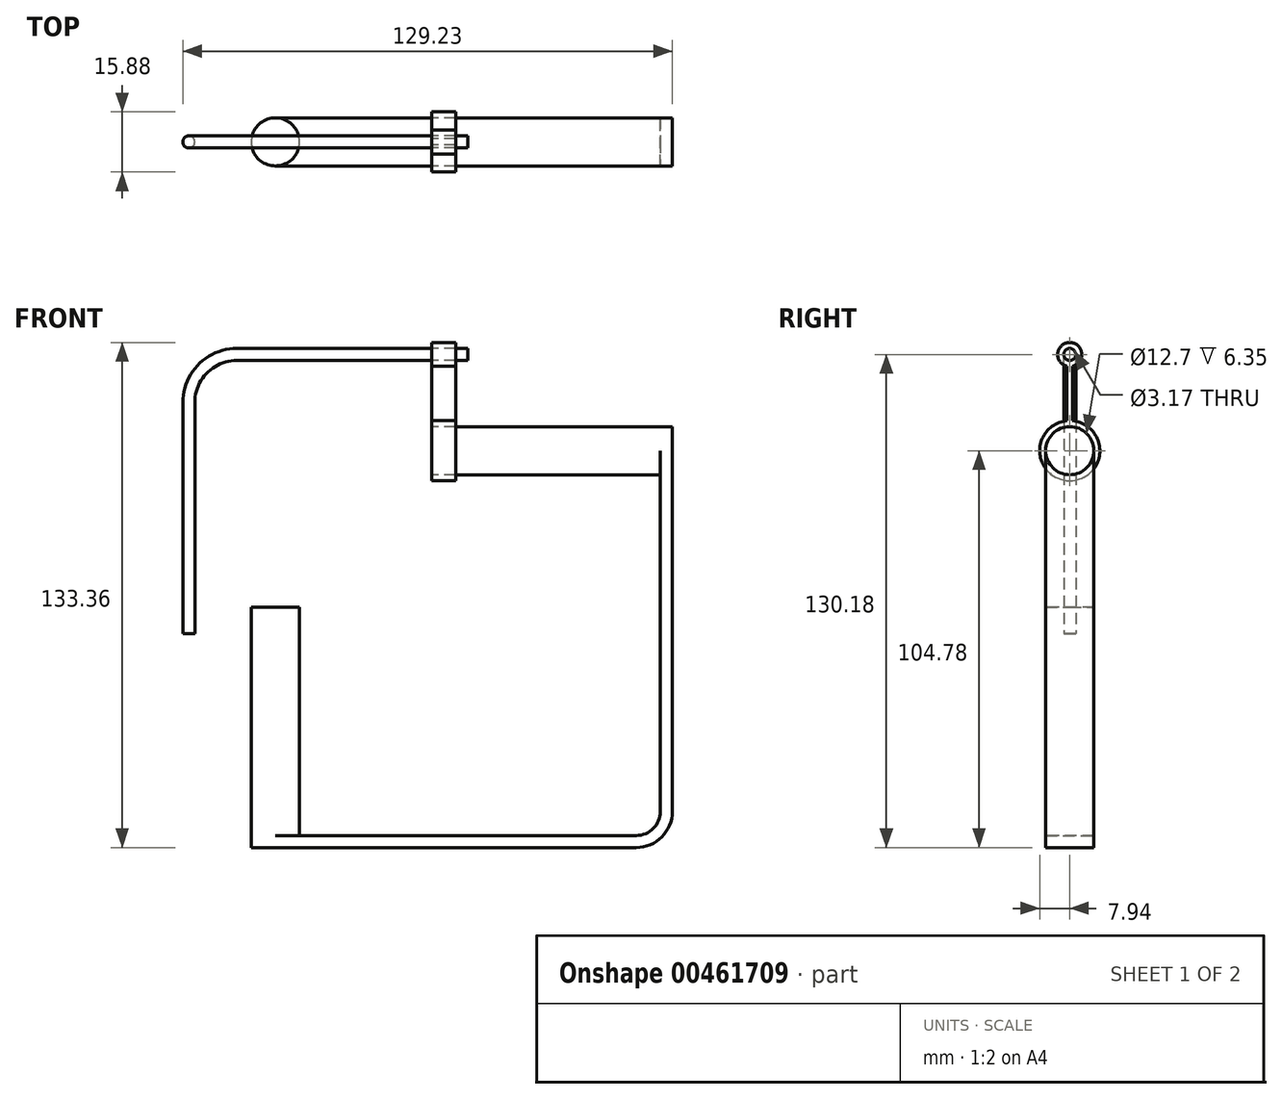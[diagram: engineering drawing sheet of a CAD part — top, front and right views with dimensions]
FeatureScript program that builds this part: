
annotation { "Feature Type Name" : "Feature", "Feature Type Description" : "" }
export const myFeature = defineFeature(function(context is Context, id is Id, definition is map)
    precondition{}
    {
        {
            var Q0;
            Q0=qCreatedBy(makeId("Front.planeOp"),FACE);
            var sketch = newSketch(context, id + "F0", { "sketchPlane" : qUnion([Q0])});
            skLineSegment(sketch, "E0", {"start": v(0, 0) * mm, "end": v(0, 101.6) * mm});
            skLineSegment(sketch, "E1", {"start": v(0, 0) * mm, "end": v(-101.6, 0) * mm});
            skLineSegment(sketch, "E2", {"start": v(0, 101.6) * mm, "end": v(3.17, 101.6) * mm});
            skLineSegment(sketch, "E3", {"start": v(3.17, 101.6) * mm, "end": v(3.18, -3.17) * mm});
            skLineSegment(sketch, "E4", {"start": v(3.18, -3.17) * mm, "end": v(-101.6, -3.18) * mm});
            skLineSegment(sketch, "E5", {"start": v(-101.6, -3.18) * mm, "end": v(-101.6, 0) * mm});
            skSolve(sketch);
        }
        {
            var Q0;
            Q0 = qSketchRegion(id + "F0", true);
            extrude(context, id + "F1", {"entities" : qUnion([Q0]), "endBound" : BoundingType.SYMMETRIC, "depth" : 12.7 * mm});
        }
        {
            var Q0;
            Q0=makeQuery(id+"F1.opExtrude","SWEPT_FACE",FACE,{"disambiguationData":[OSD([sQuery(id+"F0.wireOp",EDGE,"E3")])]});
            var sketch = newSketch(context, id + "F2", { "sketchPlane" : qUnion([Q0])});
            skCircle(sketch, "E6", {"center": v(0, 101.6) * mm, "radius": 6.35 * mm});
            skSolve(sketch);
        }
        {
            var Q0;
            Q0 = qSketchRegion(id + "F2", true);
            extrude(context, id + "F3", {"entities" : qUnion([Q0]), "operationType" : NewBodyOperationType.ADD, "oppositeDirection" : true, "depth" : 63.5 * mm});
        }
        {
            var Q0;
            Q0=makeQuery(id+"F1.opExtrude","SWEPT_FACE",FACE,{"disambiguationData":[OSD([sQuery(id+"F0.wireOp",EDGE,"E4")])]});
            var sketch = newSketch(context, id + "F4", { "sketchPlane" : qUnion([Q0])});
            skCircle(sketch, "E7", {"center": v(-101.6, 0) * mm, "radius": 6.35 * mm});
            skSolve(sketch);
        }
        {
            var Q0;
            Q0 = qSketchRegion(id + "F4", true);
            extrude(context, id + "F5", {"entities" : qUnion([Q0]), "operationType" : NewBodyOperationType.ADD, "oppositeDirection" : true, "depth" : 63.5 * mm});
        }
        {
            var Q0;
            Q0=makeQuery(id+"F3.opExtrude","CAP_FACE",FACE,{"disambiguationData":[OSD([sQuery(id+"F2.wireOp",EDGE,"E6")])],"isStart":false});
            var sketch = newSketch(context, id + "F6", { "sketchPlane" : qUnion([Q0])});
            skCircle(sketch, "E8.0", {"center": v(0, 101.6) * mm, "radius": 6.35 * mm});
            skCircle(sketch, "E9.0", {"center": v(0, 101.6) * mm, "radius": 7.94 * mm});
            skSolve(sketch);
        }
        {
            var Q0;
            Q0 = qSketchRegion(id + "F6", true);
            extrude(context, id + "F7", {"entities" : qUnion([Q0]), "oppositeDirection" : true, "depth" : 6.35 * mm});
        }
        {
            var Q0;
            Q0=makeQuery(id+"F7.opExtrude","CAP_FACE",FACE,{"disambiguationData":[OSD([sQuery(id+"F6.wireOp",EDGE,"E8.0"),sQuery(id+"F6.wireOp",EDGE,"E9.0")])],"isStart":true});
            var sketch = newSketch(context, id + "F8", { "sketchPlane" : qUnion([Q0])});
            skLineSegment(sketch, "E10", {"start": v(0, 101.6) * mm, "end": v(0, 127) * mm, "construction": true});
            skLineSegment(sketch, "E11.bottom", {"start": v(-0.8, 127) * mm, "end": v(0.8, 127) * mm});
            skLineSegment(sketch, "E11.top", {"start": v(-0.8, 109.5) * mm, "end": v(0.8, 109.5) * mm});
            skLineSegment(sketch, "E11.left", {"start": v(-0.8, 127) * mm, "end": v(-0.8, 109.5) * mm});
            skLineSegment(sketch, "E11.right", {"start": v(0.8, 127) * mm, "end": v(0.8, 109.5) * mm});
            skSolve(sketch);
        }
        {
            var Q0;
            Q0 = qSketchRegion(id + "F8", true);
            var Q1;
            Q1=makeQuery(id+"F7.opExtrude","CAP_FACE",FACE,{"disambiguationData":[OSD([sQuery(id+"F6.wireOp",EDGE,"E8.0"),sQuery(id+"F6.wireOp",EDGE,"E9.0")])],"isStart":false});
            extrude(context, id + "F9", {"entities" : qUnion([Q0]), "operationType" : NewBodyOperationType.ADD, "endBound" : BoundingType.UP_TO_SURFACE, "oppositeDirection" : true, "endBoundEntityFace" : qUnion([Q1]), "depth" : 25.4 * mm});
        }
        {
            var Q0;
            Q0=makeQuery(id+"F9.boolean.opBoolean","MERGE",FACE,{"derivedFrom":[makeQuery(id+"F7.opExtrude","CAP_FACE",FACE,{"disambiguationData":[OSD([sQuery(id+"F6.wireOp",EDGE,"E8.0"),sQuery(id+"F6.wireOp",EDGE,"E9.0")])],"isStart":true}),makeQuery(id+"F9.opExtrude","CAP_FACE",FACE,{"disambiguationData":[OSD([sQuery(id+"F8.wireOp",EDGE,"E11.bottom"),sQuery(id+"F8.wireOp",EDGE,"E11.top"),sQuery(id+"F8.wireOp",EDGE,"E11.left"),sQuery(id+"F8.wireOp",EDGE,"E11.right")])],"isStart":true})]});
            var sketch = newSketch(context, id + "F10", { "sketchPlane" : qUnion([Q0])});
            skCircle(sketch, "E12", {"center": v(0, 127) * mm, "radius": 3.18 * mm});
            skSolve(sketch);
        }
        {
            var Q0;
            Q0 = qSketchRegion(id + "F10", true);
            var Q1;
            {var subQ0=sQuery(id+"F6.wireOp",EDGE,"E9.0");var subQ1=sQuery(id+"F6.wireOp",EDGE,"E8.0");Q1=makeQuery(id+"F9.boolean.opBoolean","MERGE",FACE,{"derivedFrom":[makeQuery(id+"F7.opExtrude","CAP_FACE",FACE,{"disambiguationData":[OSD([subQ1,subQ0])],"isStart":false}),makeQuery(id+"F9.opExtrude","CAP_FACE",FACE,{"disambiguationData":[OSD([subQ1,subQ0])],"isStart":false})]});}
            extrude(context, id + "F11", {"entities" : qUnion([Q0]), "operationType" : NewBodyOperationType.ADD, "endBound" : BoundingType.UP_TO_SURFACE, "oppositeDirection" : true, "endBoundEntityFace" : qUnion([Q1]), "depth" : 25.4 * mm});
        }
        {
            var Q0;
            Q0=makeQuery(id+"F11.boolean.opBoolean","MERGE",FACE,{"derivedFrom":[makeQuery(id+"F9.boolean.opBoolean","MERGE",FACE,{"derivedFrom":[makeQuery(id+"F7.opExtrude","CAP_FACE",FACE,{"disambiguationData":[OSD([sQuery(id+"F6.wireOp",EDGE,"E8.0"),sQuery(id+"F6.wireOp",EDGE,"E9.0")])],"isStart":true}),makeQuery(id+"F9.opExtrude","CAP_FACE",FACE,{"disambiguationData":[OSD([sQuery(id+"F8.wireOp",EDGE,"E11.bottom"),sQuery(id+"F8.wireOp",EDGE,"E11.top"),sQuery(id+"F8.wireOp",EDGE,"E11.left"),sQuery(id+"F8.wireOp",EDGE,"E11.right")])],"isStart":true})]}),makeQuery(id+"F11.opExtrude","CAP_FACE",FACE,{"disambiguationData":[OSD([sQuery(id+"F10.wireOp",EDGE,"E12")])],"isStart":true})]});
            var sketch = newSketch(context, id + "F12", { "sketchPlane" : qUnion([Q0])});
            skPoint(sketch, "E13", {"position": v(0, 127) * mm});
            skSolve(sketch);
        }
        {
            var Q0;
            Q0=sQuery(id+"F12.wireOp",VERTEX,"E13");
            var Q1;
            Q1=makeQuery(id+"F7.opExtrude","SWEPT_BODY",BODY,{"disambiguationData":[OSD([sQuery(id+"F6.wireOp",EDGE,"E8.0"),sQuery(id+"F6.wireOp",EDGE,"E9.0")])]});
            hole(context, id + "F13", {"style" : HoleStyle.SIMPLE, "endStyle" : HoleEndStyle.THROUGH, "holeDiameter" : 3.17 * mm, "isTappedThrough" : true, "tappedDepth" : 12.7 * mm, "tapClearance" : 3, "locations" : qUnion([Q0]), "scope" : qUnion([Q1])});
        }
        {
            var Q0;
            Q0=qCreatedBy(makeId("Front.planeOp"),FACE);
            var sketch = newSketch(context, id + "F14", { "sketchPlane" : qUnion([Q0])});
            skLineSegment(sketch, "E14", {"start": v(-50.8, 127) * mm, "end": v(-111.76, 127) * mm});
            skLineSegment(sketch, "E15", {"start": v(-124.46, 114.3) * mm, "end": v(-124.46, 53.34) * mm});
            skLineSegment(sketch, "E16.0", {"start": v(-60.33, 125.41) * mm, "end": v(-60.33, 128.59) * mm, "construction": true});
            skLineSegment(sketch, "E17", {"start": v(-42.83, 127) * mm, "end": v(-60.33, 127) * mm, "construction": true});
            skPoint(sketch, "E18.visualSharp", {"position": v(-124.46, 127) * mm});
            skArc(sketch, "E18.filletArc", {"start": v(-111.76, 127) * mm, "mid": v(-120.74, 123.28) * mm, "end": v(-124.46, 114.3) * mm});
            skSolve(sketch);
        }
        {
            var Q0;
            Q0=sQuery(id+"F14.wireOp",EDGE,"E14");
            var Q1;
            Q1=sQuery(id+"F14.wireOp",VERTEX,"E14.start");
            cPlane(context, id + "F15", {"entities" : qUnion([Q0, Q1]), "cplaneType" : CPlaneType.CURVE_POINT, "offset" : 25.4 * mm, "width" : 152.4 * mm, "height" : 152.4 * mm});
        }
        {
            var Q0;
            Q0=qCreatedBy(id+"F15.planeOp",FACE);
            var sketch = newSketch(context, id + "F16", { "sketchPlane" : qUnion([Q0])});
            skCircle(sketch, "E19", {"center": v(0, 127) * mm, "radius": 1.59 * mm});
            skSolve(sketch);
        }
        {
            var Q0;
            Q0=makeQuery(id+"F16.imprint","IMPRINT",FACE,{"disambiguationData":[TD([[makeQuery(id+"F16.imprint","IMPRINT",EDGE,{"derivedFrom":sQuery(id+"F16.wireOp",EDGE,"E19")}),1.0]])]});
            var Q1;
            Q1=sQuery(id+"F14.wireOp",EDGE,"E14");
            var Q2;
            Q2=sQuery(id+"F14.wireOp",EDGE,"E18.filletArc");
            var Q3;
            Q3=sQuery(id+"F14.wireOp",EDGE,"E15");
            sweep(context, id + "F17", {"profiles" : qUnion([Q0]), "path" : qUnion([Q1, Q2, Q3])});
        }
        {
            var Q0;
            Q0=makeQuery(id+"F1.opExtrude","SWEPT_EDGE",EDGE,{"disambiguationData":[OSD([sQuery(id+"F0.wireOp",EDGE,"E0"),sQuery(id+"F0.wireOp",EDGE,"E1")])]});
            fillet(context, id + "F18", {"entities" : qUnion([Q0]), "radius" : 6.35 * mm, "tangentPropagation" : true, "allowEdgeOverflow" : false});
        }
        {
            var Q0;
            Q0=makeQuery(id+"F1.opExtrude","SWEPT_EDGE",EDGE,{"disambiguationData":[OSD([sQuery(id+"F0.wireOp",EDGE,"E3"),sQuery(id+"F0.wireOp",EDGE,"E4")])]});
            fillet(context, id + "F19", {"entities" : qUnion([Q0]), "radius" : 9.52 * mm, "tangentPropagation" : true, "allowEdgeOverflow" : false});
        }
    });
